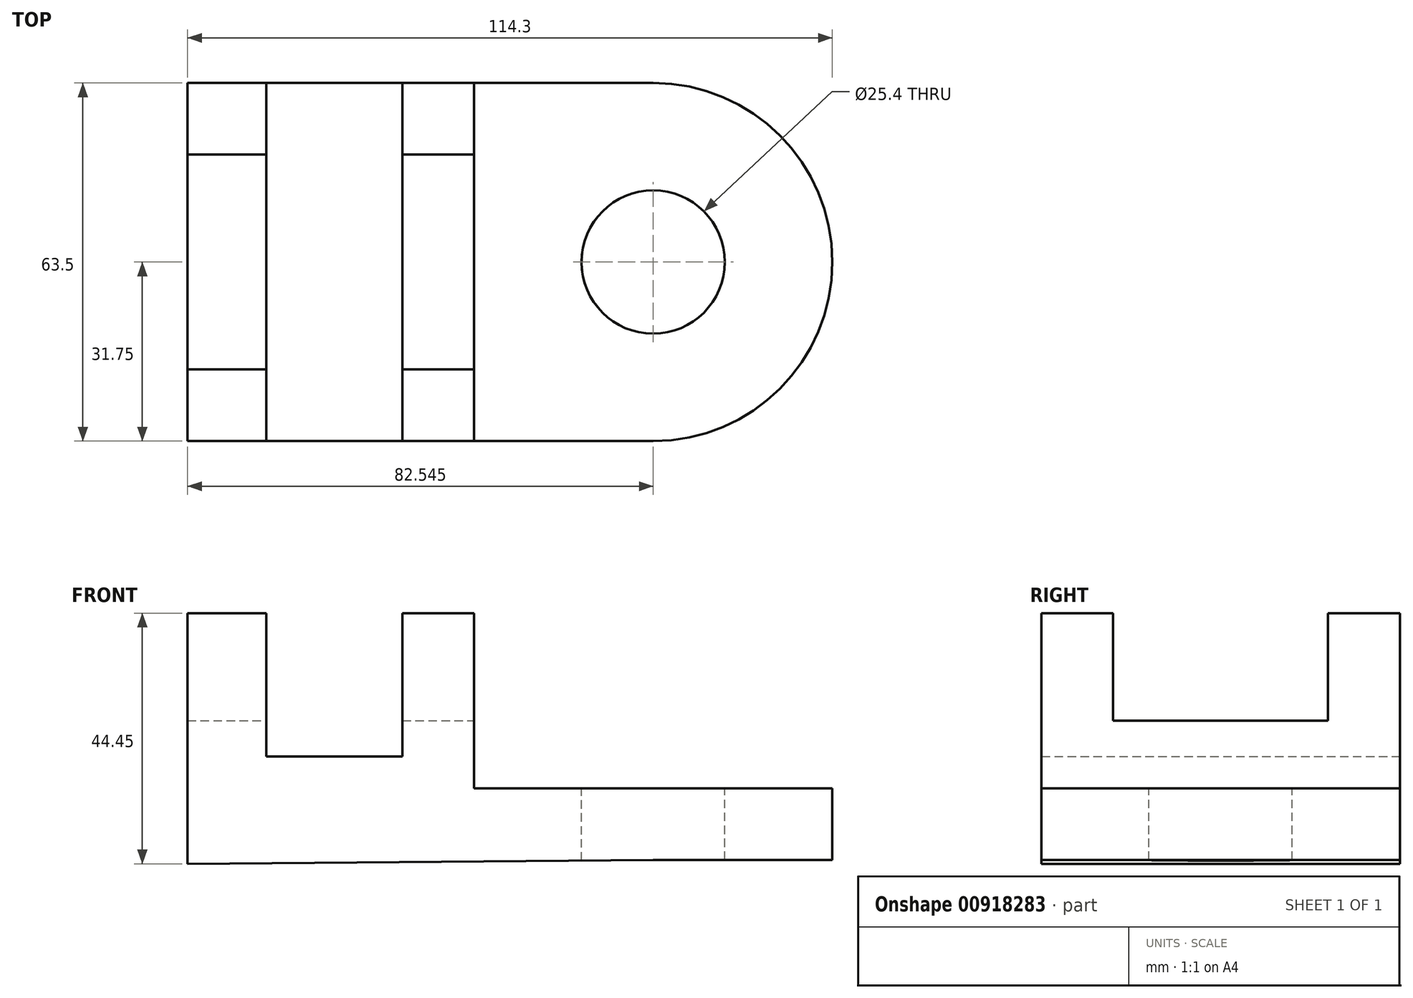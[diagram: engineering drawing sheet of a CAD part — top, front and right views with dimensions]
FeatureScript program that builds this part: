
annotation { "Feature Type Name" : "Feature", "Feature Type Description" : "" }
export const myFeature = defineFeature(function(context is Context, id is Id, definition is map)
    precondition{}
    {
        {
            var Q0;
            Q0=qCreatedBy(makeId("Front.planeOp"),FACE);
            var sketch = newSketch(context, id + "F0", { "sketchPlane" : qUnion([Q0])});
            skLineSegment(sketch, "E0", {"start": v(-8.3, 17.48) * mm, "end": v(-8.3, -26.97) * mm});
            skLineSegment(sketch, "E1", {"start": v(5.67, -7.92) * mm, "end": v(29.8, -7.92) * mm});
            skLineSegment(sketch, "E2", {"start": v(29.8, -7.92) * mm, "end": v(29.8, 17.48) * mm});
            skLineSegment(sketch, "E3", {"start": v(29.8, 17.48) * mm, "end": v(42.5, 17.48) * mm});
            skLineSegment(sketch, "E4", {"start": v(42.5, 17.48) * mm, "end": v(42.5, -13.6) * mm});
            skLineSegment(sketch, "E5", {"start": v(42.5, -13.6) * mm, "end": v(74.25, -13.6) * mm});
            skLineSegment(sketch, "E6", {"start": v(74.25, -13.6) * mm, "end": v(74.25, -26.3) * mm});
            skLineSegment(sketch, "E7", {"start": v(-8.3, -26.97) * mm, "end": v(74.25, -26.3) * mm});
            skLineSegment(sketch, "E8", {"start": v(5.67, -7.92) * mm, "end": v(5.67, 17.48) * mm});
            skLineSegment(sketch, "E9", {"start": v(-8.3, 17.48) * mm, "end": v(5.67, 17.48) * mm});
            skSolve(sketch);
        }
        {
            var Q0;
            Q0 = qSketchRegion(id + "F0", true);
            extrude(context, id + "F1", {"entities" : qUnion([Q0]), "depth" : 63.5 * mm, "offsetDistance" : 25.4 * mm});
        }
        {
            var Q0;
            Q0=makeQuery(id+"F1.opExtrude","SWEPT_FACE",FACE,{"disambiguationData":[OSD([sQuery(id+"F0.wireOp",EDGE,"E5")])]});
            var sketch = newSketch(context, id + "F2", { "sketchPlane" : qUnion([Q0])});
            skCircle(sketch, "E10", {"center": v(74.25, -31.75) * mm, "radius": 31.75 * mm});
            skSolve(sketch);
        }
        {
            var Q0;
            {var subQ1=sQuery(id+"F0.wireOp",EDGE,"E5");var subQ2=makeQuery(id+"F1.opExtrude","SWEPT_EDGE",EDGE,{"disambiguationData":[OSD([subQ1,sQuery(id+"F0.wireOp",EDGE,"E6")])]});Q0=makeQuery(id+"F2.imprint","IMPRINT",FACE,{"disambiguationData":[TD([[makeQuery(id+"F2.imprint","IMPRINT",EDGE,{"derivedFrom":subQ2}),-1.0]])]});}
            var Q1;
            Q1=makeQuery(id+"F1.opExtrude","SWEPT_BODY",BODY,{"disambiguationData":[OSD([sQuery(id+"F0.wireOp",EDGE,"E0"),sQuery(id+"F0.wireOp",EDGE,"E1"),sQuery(id+"F0.wireOp",EDGE,"E2"),sQuery(id+"F0.wireOp",EDGE,"E3"),sQuery(id+"F0.wireOp",EDGE,"E4"),sQuery(id+"F0.wireOp",EDGE,"E5"),sQuery(id+"F0.wireOp",EDGE,"E6"),sQuery(id+"F0.wireOp",EDGE,"E7"),sQuery(id+"F0.wireOp",EDGE,"E8"),sQuery(id+"F0.wireOp",EDGE,"E9")])]});
            extrude(context, id + "F3", {"entities" : qUnion([Q0]), "operationType" : NewBodyOperationType.ADD, "oppositeDirection" : true, "depth" : 12.7 * mm, "endBoundEntityBody" : qUnion([Q1]), "offsetDistance" : 25.4 * mm});
        }
        {
            var Q0;
            {var subQ0=sQuery(id+"F0.wireOp",EDGE,"E5");Q0=makeQuery(id+"F3.boolean.opBoolean","MERGE",FACE,{"derivedFrom":[makeQuery(id+"F1.opExtrude","SWEPT_FACE",FACE,{"disambiguationData":[OSD([subQ0])]}),makeQuery(id+"F3.opExtrude","CAP_FACE",FACE,{"disambiguationData":[OSD([subQ0,sQuery(id+"F0.wireOp",EDGE,"E6"),sQuery(id+"F2.wireOp",EDGE,"E10")])],"isStart":true})]});}
            var sketch = newSketch(context, id + "F4", { "sketchPlane" : qUnion([Q0])});
            skCircle(sketch, "E11", {"center": v(74.25, -31.75) * mm, "radius": 12.7 * mm});
            skSolve(sketch);
        }
        {
            var Q0;
            Q0=makeQuery(id+"F1.opExtrude","SWEPT_FACE",FACE,{"disambiguationData":[OSD([sQuery(id+"F0.wireOp",EDGE,"E4")])]});
            var sketch = newSketch(context, id + "F5", { "sketchPlane" : qUnion([Q0])});
            skLineSegment(sketch, "E12.bottom", {"start": v(-50.8, 17.48) * mm, "end": v(-12.7, 17.48) * mm});
            skLineSegment(sketch, "E12.top", {"start": v(-50.8, -1.57) * mm, "end": v(-12.7, -1.57) * mm});
            skLineSegment(sketch, "E12.left", {"start": v(-50.8, 17.48) * mm, "end": v(-50.8, -1.57) * mm});
            skLineSegment(sketch, "E12.right", {"start": v(-12.7, 17.48) * mm, "end": v(-12.7, -1.57) * mm});
            skSolve(sketch);
        }
        {
            var Q0;
            Q0=makeQuery(id+"F4.imprint","IMPRINT",FACE,{"disambiguationData":[TD([[makeQuery(id+"F4.imprint","IMPRINT",EDGE,{"derivedFrom":sQuery(id+"F4.wireOp",EDGE,"E11")}),1.0]])]});
            extrude(context, id + "F6", {"entities" : qUnion([Q0]), "operationType" : NewBodyOperationType.REMOVE, "oppositeDirection" : true, "depth" : 25.4 * mm, "offsetDistance" : 25.4 * mm});
        }
        {
            var Q0;
            Q0=makeQuery(id+"F5.imprint","IMPRINT",FACE,{"disambiguationData":[TD([[makeQuery(id+"F5.imprint","IMPRINT",EDGE,{"derivedFrom":sQuery(id+"F5.wireOp",EDGE,"E12.bottom")}),-1.0]])]});
            extrude(context, id + "F7", {"entities" : qUnion([Q0]), "operationType" : NewBodyOperationType.REMOVE, "endBound" : BoundingType.THROUGH_ALL, "oppositeDirection" : true, "depth" : 25.4 * mm, "offsetDistance" : 25.4 * mm});
        }
    });
